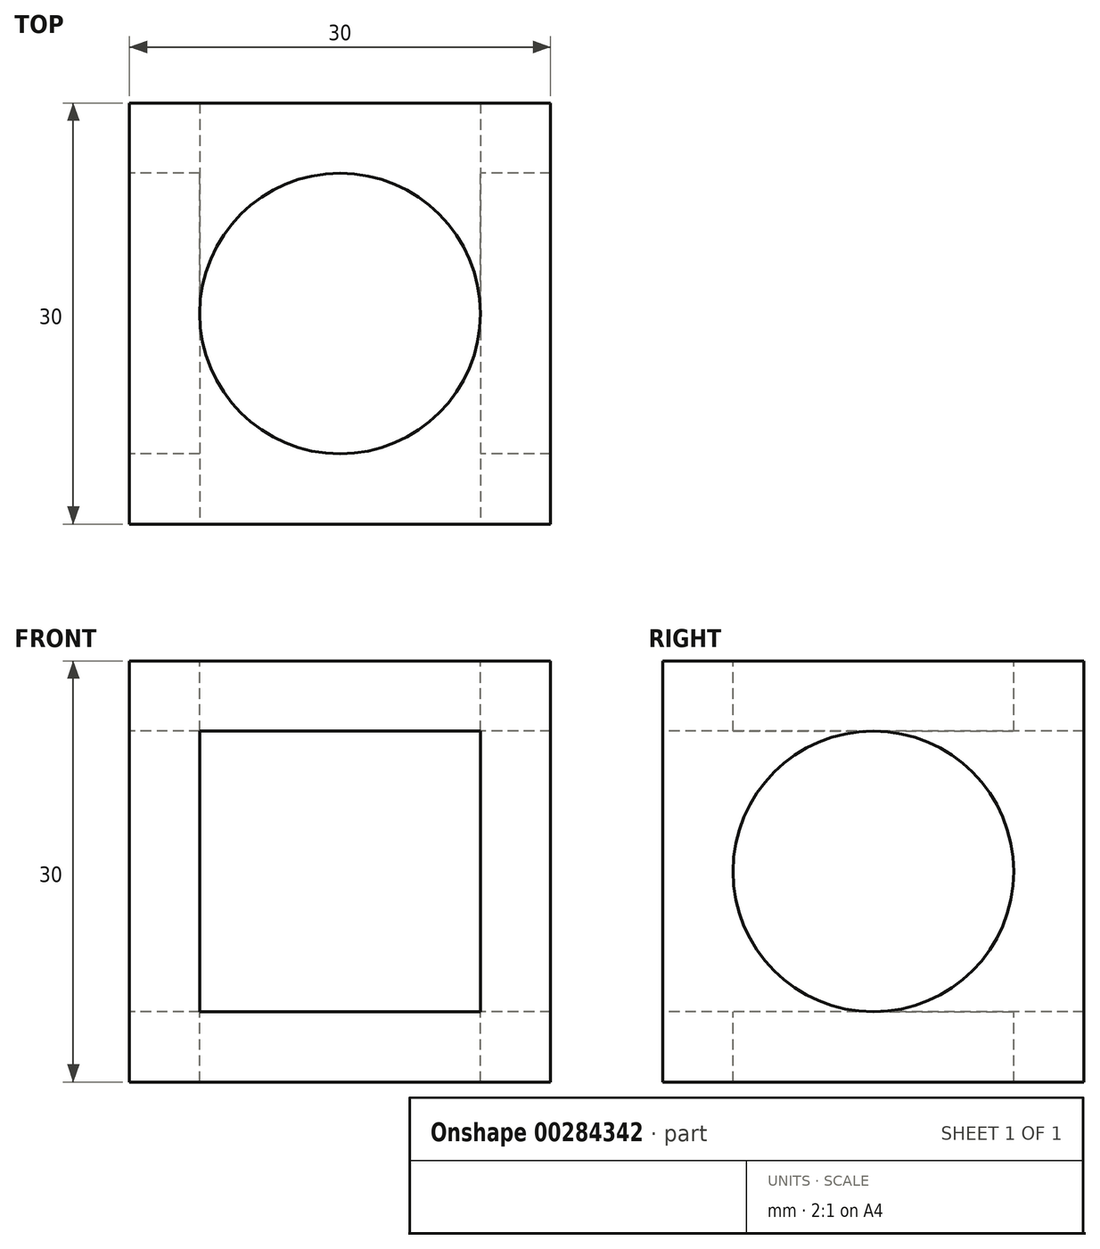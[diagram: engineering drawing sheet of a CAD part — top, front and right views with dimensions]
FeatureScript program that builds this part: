
annotation { "Feature Type Name" : "Feature", "Feature Type Description" : "" }
export const myFeature = defineFeature(function(context is Context, id is Id, definition is map)
    precondition{}
    {
        {
            var Q0;
            Q0=qCreatedBy(makeId("Front.planeOp"),FACE);
            var sketch = newSketch(context, id + "F0", { "sketchPlane" : qUnion([Q0])});
            skLineSegment(sketch, "E0.bottom", {"start": v(15, -15) * mm, "end": v(-15, -15) * mm});
            skLineSegment(sketch, "E0.top", {"start": v(15, 15) * mm, "end": v(-15, 15) * mm});
            skLineSegment(sketch, "E0.left", {"start": v(15, -15) * mm, "end": v(15, 15) * mm});
            skLineSegment(sketch, "E0.right", {"start": v(-15, -15) * mm, "end": v(-15, 15) * mm});
            skPoint(sketch, "E0.middle", {"position": v(0, 0) * mm});
            skSolve(sketch);
        }
        {
            var Q0;
            Q0=makeQuery(id+"F0.imprint","IMPRINT",FACE,{"disambiguationData":[TD([[makeQuery(id+"F0.imprint","IMPRINT",EDGE,{"derivedFrom":sQuery(id+"F0.wireOp",EDGE,"E0.bottom")}),-1.0]])]});
            extrude(context, id + "F1", {"entities" : qUnion([Q0]), "depth" : 15 * mm});
        }
        {
            var Q0;
            Q0=makeQuery(id+"F1.opExtrude","CAP_FACE",FACE,{"disambiguationData":[OSD([sQuery(id+"F0.wireOp",EDGE,"E0.bottom"),sQuery(id+"F0.wireOp",EDGE,"E0.top"),sQuery(id+"F0.wireOp",EDGE,"E0.left"),sQuery(id+"F0.wireOp",EDGE,"E0.right")])],"isStart":true});
            extrude(context, id + "F2", {"entities" : qUnion([Q0]), "operationType" : NewBodyOperationType.ADD, "depth" : 15 * mm});
        }
        {
            var Q0;
            Q0=makeQuery(id+"F1.opExtrude","CAP_FACE",FACE,{"disambiguationData":[OSD([sQuery(id+"F0.wireOp",EDGE,"E0.bottom"),sQuery(id+"F0.wireOp",EDGE,"E0.top"),sQuery(id+"F0.wireOp",EDGE,"E0.left"),sQuery(id+"F0.wireOp",EDGE,"E0.right")])],"isStart":false});
            var sketch = newSketch(context, id + "F3", { "sketchPlane" : qUnion([Q0])});
            skLineSegment(sketch, "E1.bottom", {"start": v(-10, 10) * mm, "end": v(10, 10) * mm});
            skLineSegment(sketch, "E1.top", {"start": v(-10, -10) * mm, "end": v(10, -10) * mm});
            skLineSegment(sketch, "E1.left", {"start": v(-10, 10) * mm, "end": v(-10, -10) * mm});
            skLineSegment(sketch, "E1.right", {"start": v(10, 10) * mm, "end": v(10, -10) * mm});
            skPoint(sketch, "E1.middle", {"position": v(0, 0) * mm});
            skSolve(sketch);
        }
        {
            var Q0;
            Q0=makeQuery(id+"F3.imprint","IMPRINT",FACE,{"disambiguationData":[TD([[makeQuery(id+"F3.imprint","IMPRINT",EDGE,{"derivedFrom":sQuery(id+"F3.wireOp",EDGE,"E1.bottom")}),-1.0]])]});
            extrude(context, id + "F4", {"entities" : qUnion([Q0]), "operationType" : NewBodyOperationType.REMOVE, "endBound" : BoundingType.THROUGH_ALL, "oppositeDirection" : true, "depth" : 25 * mm});
        }
        {
            var Q0;
            {var subQ0=sQuery(id+"F0.wireOp",EDGE,"E0.top");Q0=makeQuery(id+"F2.boolean.opBoolean","MERGE",FACE,{"derivedFrom":[makeQuery(id+"F1.opExtrude","SWEPT_FACE",FACE,{"disambiguationData":[OSD([subQ0])]}),makeQuery(id+"F2.opExtrude","SWEPT_FACE",FACE,{"disambiguationData":[OSD([subQ0])]})]});}
            var sketch = newSketch(context, id + "F5", { "sketchPlane" : qUnion([Q0])});
            skCircle(sketch, "E2", {"center": v(0, 0) * mm, "radius": 10 * mm});
            skSolve(sketch);
        }
        {
            var Q0;
            Q0 = qSketchRegion(id + "F5", true);
            extrude(context, id + "F6", {"entities" : qUnion([Q0]), "operationType" : NewBodyOperationType.REMOVE, "endBound" : BoundingType.THROUGH_ALL, "oppositeDirection" : true, "depth" : 25 * mm});
        }
        {
            var Q0;
            {var subQ0=sQuery(id+"F0.wireOp",EDGE,"E0.right");Q0=makeQuery(id+"F2.boolean.opBoolean","MERGE",FACE,{"derivedFrom":[makeQuery(id+"F1.opExtrude","SWEPT_FACE",FACE,{"disambiguationData":[OSD([subQ0])]}),makeQuery(id+"F2.opExtrude","SWEPT_FACE",FACE,{"disambiguationData":[OSD([subQ0])]})]});}
            var sketch = newSketch(context, id + "F7", { "sketchPlane" : qUnion([Q0])});
            skCircle(sketch, "E3", {"center": v(0, 0) * mm, "radius": 10 * mm});
            skSolve(sketch);
        }
        {
            var Q0;
            Q0 = qSketchRegion(id + "F7", true);
            extrude(context, id + "F8", {"entities" : qUnion([Q0]), "operationType" : NewBodyOperationType.REMOVE, "endBound" : BoundingType.THROUGH_ALL, "oppositeDirection" : true, "depth" : 25 * mm});
        }
    });
